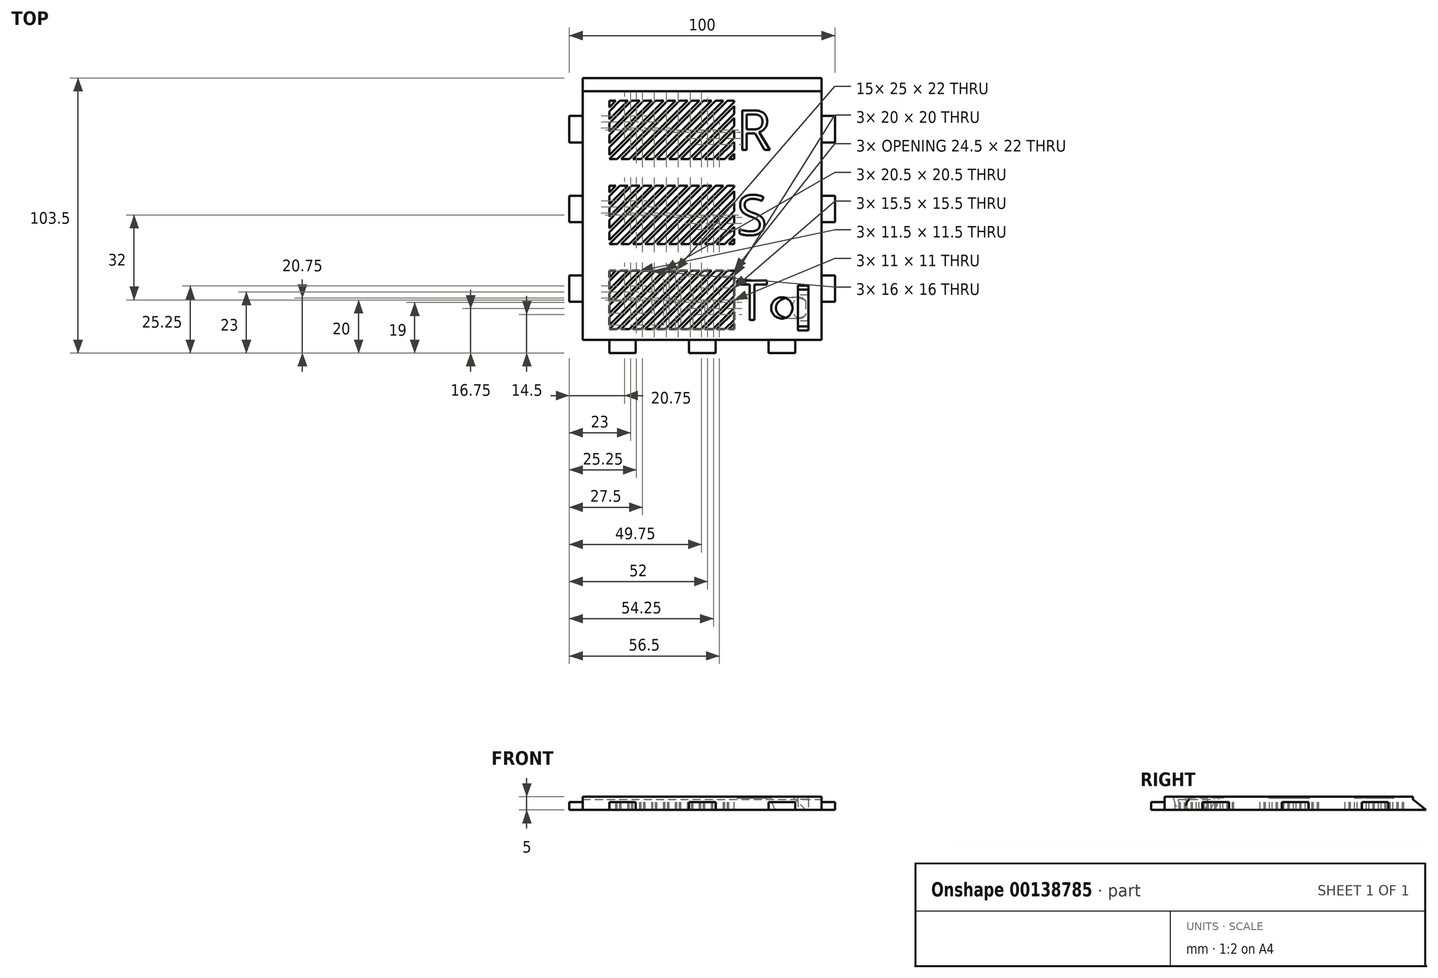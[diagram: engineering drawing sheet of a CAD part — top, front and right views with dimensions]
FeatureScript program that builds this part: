
annotation { "Feature Type Name" : "Feature", "Feature Type Description" : "" }
export const myFeature = defineFeature(function(context is Context, id is Id, definition is map)
    precondition{}
    {
        {
            var Q0;
            Q0=qCreatedBy(makeId("Top.planeOp"),FACE);
            var sketch = newSketch(context, id + "F0", { "sketchPlane" : qUnion([Q0])});
            skLineSegment(sketch, "E0.bottom", {"start": v(45, 49.25) * mm, "end": v(-45, 49.25) * mm});
            skLineSegment(sketch, "E0.top", {"start": v(45, -49.25) * mm, "end": v(-45, -49.25) * mm});
            skLineSegment(sketch, "E0.left", {"start": v(45, 49.25) * mm, "end": v(45, -49.25) * mm});
            skLineSegment(sketch, "E0.right", {"start": v(-45, 49.25) * mm, "end": v(-45, -49.25) * mm});
            skPoint(sketch, "E0.middle", {"position": v(0, 0) * mm});
            skSolve(sketch);
        }
        {
            var Q0;
            Q0 = qSketchRegion(id + "F0", true);
            extrude(context, id + "F1", {"entities" : qUnion([Q0]), "depth" : 5 * mm});
        }
        {
            var Q0;
            Q0=makeQuery(id+"F1.opExtrude","CAP_FACE",FACE,{"disambiguationData":[OSD([sQuery(id+"F0.wireOp",EDGE,"E0.bottom"),sQuery(id+"F0.wireOp",EDGE,"E0.top"),sQuery(id+"F0.wireOp",EDGE,"E0.left"),sQuery(id+"F0.wireOp",EDGE,"E0.right")])],"isStart":false});
            var sketch = newSketch(context, id + "F2", { "sketchPlane" : qUnion([Q0])});
            skLineSegment(sketch, "E1.bottom", {"start": v(-35, 40.75) * mm, "end": v(12, 40.75) * mm});
            skLineSegment(sketch, "E1.top", {"start": v(-35, 18.75) * mm, "end": v(12, 18.75) * mm});
            skLineSegment(sketch, "E1.left", {"start": v(-35, 40.75) * mm, "end": v(-35, 18.75) * mm});
            skLineSegment(sketch, "E1.right", {"start": v(12, 40.75) * mm, "end": v(12, 18.75) * mm});
            skLineSegment(sketch, "E2.bottom", {"start": v(-35, 8.75) * mm, "end": v(12, 8.75) * mm});
            skLineSegment(sketch, "E2.top", {"start": v(-35, -13.25) * mm, "end": v(12, -13.25) * mm});
            skLineSegment(sketch, "E2.left", {"start": v(-35, 8.75) * mm, "end": v(-35, -13.25) * mm});
            skLineSegment(sketch, "E2.right", {"start": v(12, 8.75) * mm, "end": v(12, -13.25) * mm});
            skLineSegment(sketch, "E3.bottom", {"start": v(-35, -23.25) * mm, "end": v(12, -23.25) * mm});
            skLineSegment(sketch, "E3.top", {"start": v(-35, -45.25) * mm, "end": v(12, -45.25) * mm});
            skLineSegment(sketch, "E3.left", {"start": v(-35, -23.25) * mm, "end": v(-35, -45.25) * mm});
            skLineSegment(sketch, "E3.right", {"start": v(12, -23.25) * mm, "end": v(12, -45.25) * mm});
            skSolve(sketch);
        }
        {
            var Q0;
            Q0=makeQuery(id+"F1.opExtrude","SWEPT_FACE",FACE,{"disambiguationData":[OSD([sQuery(id+"F0.wireOp",EDGE,"E0.right")])]});
            var sketch = newSketch(context, id + "F3", { "sketchPlane" : qUnion([Q0])});
            skLineSegment(sketch, "E4.bottom", {"start": v(-35, 0) * mm, "end": v(-25, 0) * mm});
            skLineSegment(sketch, "E4.top", {"start": v(-35, 3) * mm, "end": v(-25, 3) * mm});
            skLineSegment(sketch, "E4.left", {"start": v(-35, 0) * mm, "end": v(-35, 3) * mm});
            skLineSegment(sketch, "E4.right", {"start": v(-25, 0) * mm, "end": v(-25, 3) * mm});
            skLineSegment(sketch, "E5.bottom", {"start": v(-5, 0) * mm, "end": v(5, 0) * mm});
            skLineSegment(sketch, "E5.top", {"start": v(-5, 3) * mm, "end": v(5, 3) * mm});
            skLineSegment(sketch, "E5.left", {"start": v(-5, 0) * mm, "end": v(-5, 3) * mm});
            skLineSegment(sketch, "E5.right", {"start": v(5, 0) * mm, "end": v(5, 3) * mm});
            skLineSegment(sketch, "E6.bottom", {"start": v(25, 0) * mm, "end": v(35, 0) * mm});
            skLineSegment(sketch, "E6.top", {"start": v(25, 3) * mm, "end": v(35, 3) * mm});
            skLineSegment(sketch, "E6.left", {"start": v(25, 0) * mm, "end": v(25, 3) * mm});
            skLineSegment(sketch, "E6.right", {"start": v(35, 0) * mm, "end": v(35, 3) * mm});
            skSolve(sketch);
        }
        {
            var Q0;
            Q0 = qSketchRegion(id + "F3", true);
            extrude(context, id + "F4", {"entities" : qUnion([Q0]), "operationType" : NewBodyOperationType.ADD, "depth" : 5 * mm});
        }
        {
            var Q0;
            Q0=makeQuery(id+"F1.opExtrude","SWEPT_FACE",FACE,{"disambiguationData":[OSD([sQuery(id+"F0.wireOp",EDGE,"E0.left")])]});
            var sketch = newSketch(context, id + "F5", { "sketchPlane" : qUnion([Q0])});
            skLineSegment(sketch, "E7.bottom", {"start": v(-35, 3) * mm, "end": v(-25, 3) * mm});
            skLineSegment(sketch, "E7.top", {"start": v(-35, 0) * mm, "end": v(-25, 0) * mm});
            skLineSegment(sketch, "E7.left", {"start": v(-35, 3) * mm, "end": v(-35, 0) * mm});
            skLineSegment(sketch, "E7.right", {"start": v(-25, 3) * mm, "end": v(-25, 0) * mm});
            skLineSegment(sketch, "E8.bottom", {"start": v(-5, 3) * mm, "end": v(5, 3) * mm});
            skLineSegment(sketch, "E8.top", {"start": v(-5, 0) * mm, "end": v(5, 0) * mm});
            skLineSegment(sketch, "E8.left", {"start": v(-5, 3) * mm, "end": v(-5, 0) * mm});
            skLineSegment(sketch, "E8.right", {"start": v(5, 3) * mm, "end": v(5, 0) * mm});
            skLineSegment(sketch, "E9.bottom", {"start": v(25, 3) * mm, "end": v(35, 3) * mm});
            skLineSegment(sketch, "E9.top", {"start": v(25, 0) * mm, "end": v(35, 0) * mm});
            skLineSegment(sketch, "E9.left", {"start": v(25, 3) * mm, "end": v(25, 0) * mm});
            skLineSegment(sketch, "E9.right", {"start": v(35, 3) * mm, "end": v(35, 0) * mm});
            skSolve(sketch);
        }
        {
            var Q0;
            Q0 = qSketchRegion(id + "F5", true);
            extrude(context, id + "F6", {"entities" : qUnion([Q0]), "operationType" : NewBodyOperationType.ADD, "depth" : 5 * mm});
        }
        {
            var Q0;
            Q0=makeQuery(id+"F1.opExtrude","SWEPT_FACE",FACE,{"disambiguationData":[OSD([sQuery(id+"F0.wireOp",EDGE,"E0.top")])]});
            var sketch = newSketch(context, id + "F7", { "sketchPlane" : qUnion([Q0])});
            skLineSegment(sketch, "E10.bottom", {"start": v(-35, 0) * mm, "end": v(-25, 0) * mm});
            skLineSegment(sketch, "E10.top", {"start": v(-35, 3) * mm, "end": v(-25, 3) * mm});
            skLineSegment(sketch, "E10.left", {"start": v(-35, 0) * mm, "end": v(-35, 3) * mm});
            skLineSegment(sketch, "E10.right", {"start": v(-25, 0) * mm, "end": v(-25, 3) * mm});
            skLineSegment(sketch, "E11.bottom", {"start": v(-5, 0) * mm, "end": v(5, 0) * mm});
            skLineSegment(sketch, "E11.top", {"start": v(-5, 3) * mm, "end": v(5, 3) * mm});
            skLineSegment(sketch, "E11.left", {"start": v(-5, 0) * mm, "end": v(-5, 3) * mm});
            skLineSegment(sketch, "E11.right", {"start": v(5, 0) * mm, "end": v(5, 3) * mm});
            skLineSegment(sketch, "E12.bottom", {"start": v(25, 0) * mm, "end": v(35, 0) * mm});
            skLineSegment(sketch, "E12.top", {"start": v(25, 3) * mm, "end": v(35, 3) * mm});
            skLineSegment(sketch, "E12.left", {"start": v(25, 0) * mm, "end": v(25, 3) * mm});
            skLineSegment(sketch, "E12.right", {"start": v(35, 0) * mm, "end": v(35, 3) * mm});
            skSolve(sketch);
        }
        {
            var Q0;
            Q0 = qSketchRegion(id + "F7", true);
            extrude(context, id + "F8", {"entities" : qUnion([Q0]), "operationType" : NewBodyOperationType.ADD, "depth" : 5 * mm});
        }
        {
            var Q0;
            Q0=makeQuery(id+"F2.imprint","IMPRINT",FACE,{"disambiguationData":[TD([[makeQuery(id+"F2.imprint","IMPRINT",EDGE,{"derivedFrom":sQuery(id+"F2.wireOp",EDGE,"E1.bottom")}),-1.0]])]});
            var sketch = newSketch(context, id + "F9", { "sketchPlane" : qUnion([Q0])});
            skLineSegment(sketch, "E13", {"start": v(-35, 18.75) * mm, "end": v(-13, 40.75) * mm});
            skLineSegment(sketch, "E14", {"start": v(-13, 40.75) * mm, "end": v(-10, 40.75) * mm});
            skLineSegment(sketch, "E15", {"start": v(-10, 40.75) * mm, "end": v(-32, 18.75) * mm});
            skLineSegment(sketch, "E16", {"start": v(-32, 18.75) * mm, "end": v(-35, 18.75) * mm});
            skLineSegment(sketch, "E17.1.0.0", {"start": v(-27.5, 18.75) * mm, "end": v(-30.5, 18.75) * mm});
            skLineSegment(sketch, "E17.1.0.1", {"start": v(-5.5, 40.75) * mm, "end": v(-27.5, 18.75) * mm});
            skLineSegment(sketch, "E17.1.0.2", {"start": v(-8.5, 40.75) * mm, "end": v(-5.5, 40.75) * mm});
            skLineSegment(sketch, "E17.1.0.3", {"start": v(-30.5, 18.75) * mm, "end": v(-8.5, 40.75) * mm});
            skLineSegment(sketch, "E17.2.0.0", {"start": v(-23, 18.75) * mm, "end": v(-26, 18.75) * mm});
            skLineSegment(sketch, "E17.2.0.1", {"start": v(-1, 40.75) * mm, "end": v(-23, 18.75) * mm});
            skLineSegment(sketch, "E17.2.0.2", {"start": v(-4, 40.75) * mm, "end": v(-1, 40.75) * mm});
            skLineSegment(sketch, "E17.2.0.3", {"start": v(-26, 18.75) * mm, "end": v(-4, 40.75) * mm});
            skLineSegment(sketch, "E17.3.0.0", {"start": v(-18.5, 18.75) * mm, "end": v(-21.5, 18.75) * mm});
            skLineSegment(sketch, "E17.3.0.1", {"start": v(3.5, 40.75) * mm, "end": v(-18.5, 18.75) * mm});
            skLineSegment(sketch, "E17.3.0.2", {"start": v(0.5, 40.75) * mm, "end": v(3.5, 40.75) * mm});
            skLineSegment(sketch, "E17.3.0.3", {"start": v(-21.5, 18.75) * mm, "end": v(0.5, 40.75) * mm});
            skLineSegment(sketch, "E17.4.0.0", {"start": v(-14, 18.75) * mm, "end": v(-17, 18.75) * mm});
            skLineSegment(sketch, "E17.4.0.1", {"start": v(8, 40.75) * mm, "end": v(-14, 18.75) * mm});
            skLineSegment(sketch, "E17.4.0.2", {"start": v(5, 40.75) * mm, "end": v(8, 40.75) * mm});
            skLineSegment(sketch, "E17.4.0.3", {"start": v(-17, 18.75) * mm, "end": v(5, 40.75) * mm});
            skLineSegment(sketch, "E17.5.0.0", {"start": v(-9.5, 18.75) * mm, "end": v(-12.5, 18.75) * mm});
            skLineSegment(sketch, "E17.5.0.1", {"start": v(12, 40.25) * mm, "end": v(-9.5, 18.75) * mm});
            skLineSegment(sketch, "E17.5.0.2", {"start": v(9.5, 40.75) * mm, "end": v(12, 40.75) * mm});
            skLineSegment(sketch, "E17.5.0.3", {"start": v(-12.5, 18.75) * mm, "end": v(9.5, 40.75) * mm});
            skLineSegment(sketch, "E17.6.0.0", {"start": v(-5, 18.75) * mm, "end": v(-8, 18.75) * mm});
            skLineSegment(sketch, "E17.6.0.1", {"start": v(12, 35.75) * mm, "end": v(-5, 18.75) * mm});
            skLineSegment(sketch, "E17.6.0.3", {"start": v(-8, 18.75) * mm, "end": v(12, 38.75) * mm});
            skLineSegment(sketch, "E17.7.0.0", {"start": v(-0.5, 18.75) * mm, "end": v(-3.5, 18.75) * mm});
            skLineSegment(sketch, "E17.7.0.1", {"start": v(12, 31.25) * mm, "end": v(-0.5, 18.75) * mm});
            skLineSegment(sketch, "E17.7.0.3", {"start": v(-3.5, 18.75) * mm, "end": v(12, 34.25) * mm});
            skLineSegment(sketch, "E17.8.0.0", {"start": v(4, 18.75) * mm, "end": v(1, 18.75) * mm});
            skLineSegment(sketch, "E17.8.0.1", {"start": v(12, 26.75) * mm, "end": v(4, 18.75) * mm});
            skLineSegment(sketch, "E17.8.0.3", {"start": v(1, 18.75) * mm, "end": v(12, 29.75) * mm});
            skLineSegment(sketch, "E17.9.0.0", {"start": v(8.5, 18.75) * mm, "end": v(5.5, 18.75) * mm});
            skLineSegment(sketch, "E17.9.0.1", {"start": v(12, 22.25) * mm, "end": v(8.5, 18.75) * mm});
            skLineSegment(sketch, "E17.9.0.3", {"start": v(5.5, 18.75) * mm, "end": v(12, 25.25) * mm});
            skLineSegment(sketch, "E17.10.0.0", {"start": v(12, 18.75) * mm, "end": v(10, 18.75) * mm});
            skLineSegment(sketch, "E17.10.0.3", {"start": v(10, 18.75) * mm, "end": v(12, 20.75) * mm});
            skLineSegment(sketch, "E17.direction1", {"start": v(-35, 18.75) * mm, "end": v(-30.5, 18.75) * mm, "construction": true});
            skLineSegment(sketch, "E18.left", {"start": v(-35, 20.25) * mm, "end": v(-35, 23.25) * mm});
            skLineSegment(sketch, "E18.right", {"start": v(12, 18.75) * mm, "end": v(12, 20.75) * mm});
            skLineSegment(sketch, "E19.1.0.0", {"start": v(-17.5, 40.75) * mm, "end": v(-14.5, 40.75) * mm});
            skLineSegment(sketch, "E19.1.0.1", {"start": v(-14.5, 40.75) * mm, "end": v(-35, 20.25) * mm});
            skLineSegment(sketch, "E19.1.0.2", {"start": v(-35, 23.25) * mm, "end": v(-17.5, 40.75) * mm});
            skLineSegment(sketch, "E19.2.0.0", {"start": v(-22, 40.75) * mm, "end": v(-19, 40.75) * mm});
            skLineSegment(sketch, "E19.2.0.1", {"start": v(-19, 40.75) * mm, "end": v(-35, 24.75) * mm});
            skLineSegment(sketch, "E19.2.0.2", {"start": v(-35, 27.75) * mm, "end": v(-22, 40.75) * mm});
            skLineSegment(sketch, "E19.3.0.0", {"start": v(-26.5, 40.75) * mm, "end": v(-23.5, 40.75) * mm});
            skLineSegment(sketch, "E19.3.0.1", {"start": v(-23.5, 40.75) * mm, "end": v(-35, 29.25) * mm});
            skLineSegment(sketch, "E19.3.0.2", {"start": v(-35, 32.25) * mm, "end": v(-26.5, 40.75) * mm});
            skLineSegment(sketch, "E19.4.0.0", {"start": v(-31, 40.75) * mm, "end": v(-28, 40.75) * mm});
            skLineSegment(sketch, "E19.4.0.1", {"start": v(-28, 40.75) * mm, "end": v(-35, 33.75) * mm});
            skLineSegment(sketch, "E19.4.0.2", {"start": v(-35, 36.75) * mm, "end": v(-31, 40.75) * mm});
            skLineSegment(sketch, "E19.5.0.0", {"start": v(-35, 40.75) * mm, "end": v(-32.5, 40.75) * mm});
            skLineSegment(sketch, "E19.5.0.1", {"start": v(-32.5, 40.75) * mm, "end": v(-35, 38.25) * mm});
            skLineSegment(sketch, "E19.direction1", {"start": v(-35, 18.75) * mm, "end": v(-39.5, 18.75) * mm, "construction": true});
            skLineSegment(sketch, "E20.trimOffspring", {"start": v(-35, 24.75) * mm, "end": v(-35, 27.75) * mm});
            skLineSegment(sketch, "E21.trimOffspring", {"start": v(-35, 29.25) * mm, "end": v(-35, 32.25) * mm});
            skLineSegment(sketch, "E22.trimOffspring", {"start": v(-35, 33.75) * mm, "end": v(-35, 36.75) * mm});
            skLineSegment(sketch, "E23.trimOffspring", {"start": v(-35, 38.25) * mm, "end": v(-35, 40.75) * mm});
            skLineSegment(sketch, "E24.trimOffspring", {"start": v(12, 40.25) * mm, "end": v(12, 40.75) * mm});
            skLineSegment(sketch, "E25.trimOffspring", {"start": v(12, 35.75) * mm, "end": v(12, 38.75) * mm});
            skLineSegment(sketch, "E26.trimOffspring", {"start": v(12, 31.25) * mm, "end": v(12, 34.25) * mm});
            skLineSegment(sketch, "E27.trimOffspring", {"start": v(12, 26.75) * mm, "end": v(12, 29.75) * mm});
            skLineSegment(sketch, "E28.trimOffspring", {"start": v(12, 22.25) * mm, "end": v(12, 25.25) * mm});
            skLineSegment(sketch, "E29.0.1.0", {"start": v(-35, -4.25) * mm, "end": v(-22, 8.75) * mm});
            skLineSegment(sketch, "E29.0.1.1", {"start": v(-3.5, -13.25) * mm, "end": v(12, 2.25) * mm});
            skLineSegment(sketch, "E29.0.1.2", {"start": v(-30.5, -13.25) * mm, "end": v(-8.5, 8.75) * mm});
            skLineSegment(sketch, "E29.0.1.3", {"start": v(-17, -13.25) * mm, "end": v(5, 8.75) * mm});
            skLineSegment(sketch, "E29.0.1.4", {"start": v(-23.5, 8.75) * mm, "end": v(-35, -2.75) * mm});
            skLineSegment(sketch, "E29.0.1.5", {"start": v(12, 8.25) * mm, "end": v(-9.5, -13.25) * mm});
            skLineSegment(sketch, "E29.0.1.6", {"start": v(12, -0.75) * mm, "end": v(-0.5, -13.25) * mm});
            skLineSegment(sketch, "E29.0.1.7", {"start": v(-8, -13.25) * mm, "end": v(12, 6.75) * mm});
            skLineSegment(sketch, "E29.0.1.8", {"start": v(-14.5, 8.75) * mm, "end": v(-35, -11.75) * mm});
            skLineSegment(sketch, "E29.0.1.9", {"start": v(-26, -13.25) * mm, "end": v(-4, 8.75) * mm});
            skLineSegment(sketch, "E29.0.1.10", {"start": v(-19, 8.75) * mm, "end": v(-35, -7.25) * mm});
            skLineSegment(sketch, "E29.0.1.11", {"start": v(5.5, -13.25) * mm, "end": v(12, -6.75) * mm});
            skLineSegment(sketch, "E29.0.1.12", {"start": v(-10, 8.75) * mm, "end": v(-32, -13.25) * mm});
            skLineSegment(sketch, "E29.0.1.13", {"start": v(-35, -8.75) * mm, "end": v(-17.5, 8.75) * mm});
            skLineSegment(sketch, "E29.0.1.14", {"start": v(-1, 8.75) * mm, "end": v(-23, -13.25) * mm});
            skLineSegment(sketch, "E29.0.1.15", {"start": v(-35, 4.75) * mm, "end": v(-31, 8.75) * mm});
            skLineSegment(sketch, "E29.0.1.16", {"start": v(-35, -13.25) * mm, "end": v(-13, 8.75) * mm});
            skLineSegment(sketch, "E29.0.1.17", {"start": v(-5.5, 8.75) * mm, "end": v(-27.5, -13.25) * mm});
            skLineSegment(sketch, "E29.0.1.18", {"start": v(-28, 8.75) * mm, "end": v(-35, 1.75) * mm});
            skLineSegment(sketch, "E29.0.1.19", {"start": v(-21.5, -13.25) * mm, "end": v(0.5, 8.75) * mm});
            skLineSegment(sketch, "E29.0.1.20", {"start": v(3.5, 8.75) * mm, "end": v(-18.5, -13.25) * mm});
            skLineSegment(sketch, "E29.0.1.21", {"start": v(12, -5.25) * mm, "end": v(4, -13.25) * mm});
            skLineSegment(sketch, "E29.0.1.22", {"start": v(1, -13.25) * mm, "end": v(12, -2.25) * mm});
            skLineSegment(sketch, "E29.0.1.23", {"start": v(-12.5, -13.25) * mm, "end": v(9.5, 8.75) * mm});
            skLineSegment(sketch, "E29.0.1.24", {"start": v(-35, 0.25) * mm, "end": v(-26.5, 8.75) * mm});
            skLineSegment(sketch, "E29.0.1.25", {"start": v(8, 8.75) * mm, "end": v(-14, -13.25) * mm});
            skLineSegment(sketch, "E29.0.1.26", {"start": v(12, -9.75) * mm, "end": v(8.5, -13.25) * mm});
            skLineSegment(sketch, "E29.0.1.27", {"start": v(12, 3.75) * mm, "end": v(-5, -13.25) * mm});
            skLineSegment(sketch, "E29.0.1.28", {"start": v(-32.5, 8.75) * mm, "end": v(-35, 6.25) * mm});
            skLineSegment(sketch, "E29.0.1.29", {"start": v(-26.5, 8.75) * mm, "end": v(-23.5, 8.75) * mm});
            skLineSegment(sketch, "E29.0.1.30", {"start": v(12, -5.25) * mm, "end": v(12, -2.25) * mm});
            skLineSegment(sketch, "E29.0.1.31", {"start": v(4, -13.25) * mm, "end": v(1, -13.25) * mm});
            skLineSegment(sketch, "E29.0.1.32", {"start": v(-35, 8.75) * mm, "end": v(-32.5, 8.75) * mm});
            skLineSegment(sketch, "E29.0.1.33", {"start": v(12, -0.75) * mm, "end": v(12, 2.25) * mm});
            skLineSegment(sketch, "E29.0.1.34", {"start": v(-4, 8.75) * mm, "end": v(-1, 8.75) * mm});
            skLineSegment(sketch, "E29.0.1.35", {"start": v(-23, -13.25) * mm, "end": v(-26, -13.25) * mm});
            skLineSegment(sketch, "E29.0.1.36", {"start": v(9.5, 8.75) * mm, "end": v(12, 8.75) * mm});
            skLineSegment(sketch, "E29.0.1.37", {"start": v(-27.5, -13.25) * mm, "end": v(-30.5, -13.25) * mm});
            skLineSegment(sketch, "E29.0.1.38", {"start": v(10, -13.25) * mm, "end": v(12, -11.25) * mm});
            skLineSegment(sketch, "E29.0.1.39", {"start": v(-22, 8.75) * mm, "end": v(-19, 8.75) * mm});
            skLineSegment(sketch, "E29.0.1.40", {"start": v(-35, 1.75) * mm, "end": v(-35, 4.75) * mm});
            skLineSegment(sketch, "E29.0.1.41", {"start": v(-18.5, -13.25) * mm, "end": v(-21.5, -13.25) * mm});
            skLineSegment(sketch, "E29.0.1.42", {"start": v(-9.5, -13.25) * mm, "end": v(-12.5, -13.25) * mm});
            skLineSegment(sketch, "E29.0.1.43", {"start": v(-35, 6.25) * mm, "end": v(-35, 8.75) * mm});
            skLineSegment(sketch, "E29.0.1.44", {"start": v(-0.5, -13.25) * mm, "end": v(-3.5, -13.25) * mm});
            skLineSegment(sketch, "E29.0.1.45", {"start": v(-13, 8.75) * mm, "end": v(-10, 8.75) * mm});
            skLineSegment(sketch, "E29.0.1.46", {"start": v(12, 3.75) * mm, "end": v(12, 6.75) * mm});
            skLineSegment(sketch, "E29.0.1.47", {"start": v(-8.5, 8.75) * mm, "end": v(-5.5, 8.75) * mm});
            skLineSegment(sketch, "E29.0.1.48", {"start": v(0.5, 8.75) * mm, "end": v(3.5, 8.75) * mm});
            skLineSegment(sketch, "E29.0.1.49", {"start": v(12, -9.75) * mm, "end": v(12, -6.75) * mm});
            skLineSegment(sketch, "E29.0.1.50", {"start": v(-35, -13.25) * mm, "end": v(-30.5, -13.25) * mm, "construction": true});
            skLineSegment(sketch, "E29.0.1.51", {"start": v(-14, -13.25) * mm, "end": v(-17, -13.25) * mm});
            skLineSegment(sketch, "E29.0.1.52", {"start": v(-35, -11.75) * mm, "end": v(-35, -8.75) * mm});
            skLineSegment(sketch, "E29.0.1.53", {"start": v(8.5, -13.25) * mm, "end": v(5.5, -13.25) * mm});
            skLineSegment(sketch, "E29.0.1.54", {"start": v(12, -13.25) * mm, "end": v(12, -11.25) * mm});
            skLineSegment(sketch, "E29.0.1.55", {"start": v(-5, -13.25) * mm, "end": v(-8, -13.25) * mm});
            skLineSegment(sketch, "E29.0.1.56", {"start": v(-35, -7.25) * mm, "end": v(-35, -4.25) * mm});
            skLineSegment(sketch, "E29.0.1.57", {"start": v(-31, 8.75) * mm, "end": v(-28, 8.75) * mm});
            skLineSegment(sketch, "E29.0.1.58", {"start": v(5, 8.75) * mm, "end": v(8, 8.75) * mm});
            skLineSegment(sketch, "E29.0.1.59", {"start": v(-17.5, 8.75) * mm, "end": v(-14.5, 8.75) * mm});
            skLineSegment(sketch, "E29.0.1.60", {"start": v(-35, -2.75) * mm, "end": v(-35, 0.25) * mm});
            skLineSegment(sketch, "E29.0.1.61", {"start": v(12, -13.25) * mm, "end": v(10, -13.25) * mm});
            skLineSegment(sketch, "E29.0.1.62", {"start": v(-32, -13.25) * mm, "end": v(-35, -13.25) * mm});
            skLineSegment(sketch, "E29.0.1.63", {"start": v(12, 8.25) * mm, "end": v(12, 8.75) * mm});
            skLineSegment(sketch, "E29.0.2.0", {"start": v(-35, -36.25) * mm, "end": v(-22, -23.25) * mm});
            skLineSegment(sketch, "E29.0.2.1", {"start": v(-3.5, -45.25) * mm, "end": v(12, -29.75) * mm});
            skLineSegment(sketch, "E29.0.2.2", {"start": v(-30.5, -45.25) * mm, "end": v(-8.5, -23.25) * mm});
            skLineSegment(sketch, "E29.0.2.3", {"start": v(-17, -45.25) * mm, "end": v(5, -23.25) * mm});
            skLineSegment(sketch, "E29.0.2.4", {"start": v(-23.5, -23.25) * mm, "end": v(-35, -34.75) * mm});
            skLineSegment(sketch, "E29.0.2.5", {"start": v(12, -23.75) * mm, "end": v(-9.5, -45.25) * mm});
            skLineSegment(sketch, "E29.0.2.6", {"start": v(12, -32.75) * mm, "end": v(-0.5, -45.25) * mm});
            skLineSegment(sketch, "E29.0.2.7", {"start": v(-8, -45.25) * mm, "end": v(12, -25.25) * mm});
            skLineSegment(sketch, "E29.0.2.8", {"start": v(-14.5, -23.25) * mm, "end": v(-35, -43.75) * mm});
            skLineSegment(sketch, "E29.0.2.9", {"start": v(-26, -45.25) * mm, "end": v(-4, -23.25) * mm});
            skLineSegment(sketch, "E29.0.2.10", {"start": v(-19, -23.25) * mm, "end": v(-35, -39.25) * mm});
            skLineSegment(sketch, "E29.0.2.11", {"start": v(5.5, -45.25) * mm, "end": v(12, -38.75) * mm});
            skLineSegment(sketch, "E29.0.2.12", {"start": v(-10, -23.25) * mm, "end": v(-32, -45.25) * mm});
            skLineSegment(sketch, "E29.0.2.13", {"start": v(-35, -40.75) * mm, "end": v(-17.5, -23.25) * mm});
            skLineSegment(sketch, "E29.0.2.14", {"start": v(-1, -23.25) * mm, "end": v(-23, -45.25) * mm});
            skLineSegment(sketch, "E29.0.2.15", {"start": v(-35, -27.25) * mm, "end": v(-31, -23.25) * mm});
            skLineSegment(sketch, "E29.0.2.16", {"start": v(-35, -45.25) * mm, "end": v(-13, -23.25) * mm});
            skLineSegment(sketch, "E29.0.2.17", {"start": v(-5.5, -23.25) * mm, "end": v(-27.5, -45.25) * mm});
            skLineSegment(sketch, "E29.0.2.18", {"start": v(-28, -23.25) * mm, "end": v(-35, -30.25) * mm});
            skLineSegment(sketch, "E29.0.2.19", {"start": v(-21.5, -45.25) * mm, "end": v(0.5, -23.25) * mm});
            skLineSegment(sketch, "E29.0.2.20", {"start": v(3.5, -23.25) * mm, "end": v(-18.5, -45.25) * mm});
            skLineSegment(sketch, "E29.0.2.21", {"start": v(12, -37.25) * mm, "end": v(4, -45.25) * mm});
            skLineSegment(sketch, "E29.0.2.22", {"start": v(1, -45.25) * mm, "end": v(12, -34.25) * mm});
            skLineSegment(sketch, "E29.0.2.23", {"start": v(-12.5, -45.25) * mm, "end": v(9.5, -23.25) * mm});
            skLineSegment(sketch, "E29.0.2.24", {"start": v(-35, -31.75) * mm, "end": v(-26.5, -23.25) * mm});
            skLineSegment(sketch, "E29.0.2.25", {"start": v(8, -23.25) * mm, "end": v(-14, -45.25) * mm});
            skLineSegment(sketch, "E29.0.2.26", {"start": v(12, -41.75) * mm, "end": v(8.5, -45.25) * mm});
            skLineSegment(sketch, "E29.0.2.27", {"start": v(12, -28.25) * mm, "end": v(-5, -45.25) * mm});
            skLineSegment(sketch, "E29.0.2.28", {"start": v(-32.5, -23.25) * mm, "end": v(-35, -25.75) * mm});
            skLineSegment(sketch, "E29.0.2.29", {"start": v(-26.5, -23.25) * mm, "end": v(-23.5, -23.25) * mm});
            skLineSegment(sketch, "E29.0.2.30", {"start": v(12, -37.25) * mm, "end": v(12, -34.25) * mm});
            skLineSegment(sketch, "E29.0.2.31", {"start": v(4, -45.25) * mm, "end": v(1, -45.25) * mm});
            skLineSegment(sketch, "E29.0.2.32", {"start": v(-35, -23.25) * mm, "end": v(-32.5, -23.25) * mm});
            skLineSegment(sketch, "E29.0.2.33", {"start": v(12, -32.75) * mm, "end": v(12, -29.75) * mm});
            skLineSegment(sketch, "E29.0.2.34", {"start": v(-4, -23.25) * mm, "end": v(-1, -23.25) * mm});
            skLineSegment(sketch, "E29.0.2.35", {"start": v(-23, -45.25) * mm, "end": v(-26, -45.25) * mm});
            skLineSegment(sketch, "E29.0.2.36", {"start": v(9.5, -23.25) * mm, "end": v(12, -23.25) * mm});
            skLineSegment(sketch, "E29.0.2.37", {"start": v(-27.5, -45.25) * mm, "end": v(-30.5, -45.25) * mm});
            skLineSegment(sketch, "E29.0.2.38", {"start": v(10, -45.25) * mm, "end": v(12, -43.25) * mm});
            skLineSegment(sketch, "E29.0.2.39", {"start": v(-22, -23.25) * mm, "end": v(-19, -23.25) * mm});
            skLineSegment(sketch, "E29.0.2.40", {"start": v(-35, -30.25) * mm, "end": v(-35, -27.25) * mm});
            skLineSegment(sketch, "E29.0.2.41", {"start": v(-18.5, -45.25) * mm, "end": v(-21.5, -45.25) * mm});
            skLineSegment(sketch, "E29.0.2.42", {"start": v(-9.5, -45.25) * mm, "end": v(-12.5, -45.25) * mm});
            skLineSegment(sketch, "E29.0.2.43", {"start": v(-35, -25.75) * mm, "end": v(-35, -23.25) * mm});
            skLineSegment(sketch, "E29.0.2.44", {"start": v(-0.5, -45.25) * mm, "end": v(-3.5, -45.25) * mm});
            skLineSegment(sketch, "E29.0.2.45", {"start": v(-13, -23.25) * mm, "end": v(-10, -23.25) * mm});
            skLineSegment(sketch, "E29.0.2.46", {"start": v(12, -28.25) * mm, "end": v(12, -25.25) * mm});
            skLineSegment(sketch, "E29.0.2.47", {"start": v(-8.5, -23.25) * mm, "end": v(-5.5, -23.25) * mm});
            skLineSegment(sketch, "E29.0.2.48", {"start": v(0.5, -23.25) * mm, "end": v(3.5, -23.25) * mm});
            skLineSegment(sketch, "E29.0.2.49", {"start": v(12, -41.75) * mm, "end": v(12, -38.75) * mm});
            skLineSegment(sketch, "E29.0.2.50", {"start": v(-35, -45.25) * mm, "end": v(-30.5, -45.25) * mm, "construction": true});
            skLineSegment(sketch, "E29.0.2.51", {"start": v(-14, -45.25) * mm, "end": v(-17, -45.25) * mm});
            skLineSegment(sketch, "E29.0.2.52", {"start": v(-35, -43.75) * mm, "end": v(-35, -40.75) * mm});
            skLineSegment(sketch, "E29.0.2.53", {"start": v(8.5, -45.25) * mm, "end": v(5.5, -45.25) * mm});
            skLineSegment(sketch, "E29.0.2.54", {"start": v(12, -45.25) * mm, "end": v(12, -43.25) * mm});
            skLineSegment(sketch, "E29.0.2.55", {"start": v(-5, -45.25) * mm, "end": v(-8, -45.25) * mm});
            skLineSegment(sketch, "E29.0.2.56", {"start": v(-35, -39.25) * mm, "end": v(-35, -36.25) * mm});
            skLineSegment(sketch, "E29.0.2.57", {"start": v(-31, -23.25) * mm, "end": v(-28, -23.25) * mm});
            skLineSegment(sketch, "E29.0.2.58", {"start": v(5, -23.25) * mm, "end": v(8, -23.25) * mm});
            skLineSegment(sketch, "E29.0.2.59", {"start": v(-17.5, -23.25) * mm, "end": v(-14.5, -23.25) * mm});
            skLineSegment(sketch, "E29.0.2.60", {"start": v(-35, -34.75) * mm, "end": v(-35, -31.75) * mm});
            skLineSegment(sketch, "E29.0.2.61", {"start": v(12, -45.25) * mm, "end": v(10, -45.25) * mm});
            skLineSegment(sketch, "E29.0.2.62", {"start": v(-32, -45.25) * mm, "end": v(-35, -45.25) * mm});
            skLineSegment(sketch, "E29.0.2.63", {"start": v(12, -23.75) * mm, "end": v(12, -23.25) * mm});
            skLineSegment(sketch, "E29.direction1", {"start": v(-35, 18.75) * mm, "end": v(-10, 18.75) * mm, "construction": true});
            skLineSegment(sketch, "E29.direction2", {"start": v(-35, 18.75) * mm, "end": v(-35, -13.25) * mm, "construction": true});
            skSolve(sketch);
        }
        {
            var Q0;
            Q0 = qSketchRegion(id + "F9", true);
            extrude(context, id + "F10", {"entities" : qUnion([Q0]), "operationType" : NewBodyOperationType.REMOVE, "oppositeDirection" : true, "depth" : 25 * mm});
        }
        {
            var Q0;
            Q0=makeQuery(id+"F1.opExtrude","CAP_FACE",FACE,{"disambiguationData":[OSD([sQuery(id+"F0.wireOp",EDGE,"E0.bottom"),sQuery(id+"F0.wireOp",EDGE,"E0.top"),sQuery(id+"F0.wireOp",EDGE,"E0.left"),sQuery(id+"F0.wireOp",EDGE,"E0.right")])],"isStart":false});
            var sketch = newSketch(context, id + "F11", { "sketchPlane" : qUnion([Q0])});
            skText(sketch, "E30", { "text": "R", "fontName": "OpenSans-Regular.ttf"});
            skText(sketch, "E31", { "text": "S\n", "fontName": "OpenSans-Regular.ttf"});
            skText(sketch, "E32", { "text": "T", "fontName": "OpenSans-Regular.ttf"});
            const initialGuessF11  = {"E30": [0.013, 0.02225, 1, 0, 0.015], "E31": [0.013, -0.00975, 1, 0, 0.015], "E32": [0.013, -0.04175, 1, 0, 0.015]};
            skSetInitialGuess(sketch, initialGuessF11);
            skSolve(sketch);
        }
        {
            var Q0;
            Q0 = qSketchRegion(id + "F11", true);
            extrude(context, id + "F12", {"entities" : qUnion([Q0]), "operationType" : NewBodyOperationType.REMOVE, "oppositeDirection" : true, "depth" : 0.5 * mm});
        }
        {
            var Q0;
            {var subQ0=sQuery(id+"F0.wireOp",EDGE,"E0.right");var subQ1=sQuery(id+"F0.wireOp",EDGE,"E0.left");var subQ2=sQuery(id+"F0.wireOp",EDGE,"E0.bottom");var subQ3=sQuery(id+"F0.wireOp",EDGE,"E0.top");Q0=makeQuery(id+"F12.boolean.opBoolean","SPLIT",FACE,{"disambiguationData":[TD([makeQuery(id+"F1.opExtrude","SWEPT_FACE",FACE,{"disambiguationData":[OSD([subQ2])]})])],"derivedFrom":makeQuery(id+"F1.opExtrude","CAP_FACE",FACE,{"disambiguationData":[OSD([subQ2,subQ3,subQ1,subQ0])],"isStart":false})});}
            var sketch = newSketch(context, id + "F13", { "sketchPlane" : qUnion([Q0])});
            skCircle(sketch, "E33", {"center": v(30, -37.27) * mm, "radius": 4 * mm});
            skLineSegment(sketch, "E34", {"start": v(34, -49.25) * mm, "end": v(34, -34.45) * mm});
            skSolve(sketch);
        }
        {
            var Q0;
            Q0=makeQuery(id+"F13.imprint","IMPRINT",FACE,{"disambiguationData":[TD([[makeQuery(id+"F13.imprint","IMPRINT",EDGE,{"derivedFrom":sQuery(id+"F13.wireOp",EDGE,"E33")}),1.0]])]});
            var Q1;
            Q1=sQuery(id+"F13.wireOp",EDGE,"E34");
            revolve(context, id + "F14", {"operationType" : NewBodyOperationType.REMOVE, "entities" : qUnion([Q0]), "axis" : qUnion([Q1]), "revolveType" : RevolveType.ONE_DIRECTION, "oppositeDirection" : true, "angle" : 135 * degree});
        }
        {
            var Q0;
            {var subQ0=sQuery(id+"F0.wireOp",EDGE,"E0.right");var subQ1=sQuery(id+"F0.wireOp",EDGE,"E0.left");var subQ2=sQuery(id+"F0.wireOp",EDGE,"E0.bottom");var subQ3=sQuery(id+"F0.wireOp",EDGE,"E0.top");Q0=makeQuery(id+"F12.boolean.opBoolean","SPLIT",FACE,{"disambiguationData":[TD([makeQuery(id+"F1.opExtrude","SWEPT_FACE",FACE,{"disambiguationData":[OSD([subQ2])]})])],"derivedFrom":makeQuery(id+"F1.opExtrude","CAP_FACE",FACE,{"disambiguationData":[OSD([subQ2,subQ3,subQ1,subQ0])],"isStart":false})});}
            var sketch = newSketch(context, id + "F15", { "sketchPlane" : qUnion([Q0])});
            skLineSegment(sketch, "E35.bottom", {"start": v(36, -28.77) * mm, "end": v(40, -28.77) * mm});
            skLineSegment(sketch, "E35.top", {"start": v(36, -30.27) * mm, "end": v(40, -30.27) * mm});
            skLineSegment(sketch, "E35.left", {"start": v(36, -28.77) * mm, "end": v(36, -30.27) * mm});
            skLineSegment(sketch, "E35.right", {"start": v(40, -28.77) * mm, "end": v(40, -30.27) * mm});
            skLineSegment(sketch, "E36", {"start": v(34, -37.27) * mm, "end": v(47.47, -37.27) * mm});
            skSolve(sketch);
        }
        {
            var Q0;
            Q0=makeQuery(id+"F15.imprint","IMPRINT",FACE,{"disambiguationData":[TD([[makeQuery(id+"F15.imprint","IMPRINT",EDGE,{"derivedFrom":sQuery(id+"F15.wireOp",EDGE,"E35.bottom")}),-1.0]])]});
            var Q1;
            Q1=sQuery(id+"F15.wireOp",EDGE,"E36");
            revolve(context, id + "F16", {"operationType" : NewBodyOperationType.REMOVE, "entities" : qUnion([Q0]), "axis" : qUnion([Q1]), "revolveType" : RevolveType.FULL});
        }
        {
            var Q0;
            {var subQ0=sQuery(id+"F0.wireOp",EDGE,"E0.right");var subQ1=sQuery(id+"F0.wireOp",EDGE,"E0.left");var subQ2=sQuery(id+"F0.wireOp",EDGE,"E0.bottom");var subQ3=sQuery(id+"F0.wireOp",EDGE,"E0.top");Q0=makeQuery(id+"F12.boolean.opBoolean","SPLIT",FACE,{"disambiguationData":[TD([makeQuery(id+"F1.opExtrude","SWEPT_FACE",FACE,{"disambiguationData":[OSD([subQ2])]})])],"derivedFrom":makeQuery(id+"F1.opExtrude","CAP_FACE",FACE,{"disambiguationData":[OSD([subQ2,subQ3,subQ1,subQ0])],"isStart":false})});}
            var sketch = newSketch(context, id + "F17", { "sketchPlane" : qUnion([Q0])});
            skLineSegment(sketch, "E37.bottom", {"start": v(36, -28.77) * mm, "end": v(40, -28.77) * mm});
            skLineSegment(sketch, "E37.top", {"start": v(36, -45.77) * mm, "end": v(40, -45.77) * mm});
            skLineSegment(sketch, "E37.left", {"start": v(36, -28.77) * mm, "end": v(36, -45.77) * mm});
            skLineSegment(sketch, "E37.right", {"start": v(40, -28.77) * mm, "end": v(40, -45.77) * mm});
            skSolve(sketch);
        }
        {
            var Q0;
            Q0 = qSketchRegion(id + "F17", true);
            extrude(context, id + "F18", {"entities" : qUnion([Q0]), "operationType" : NewBodyOperationType.REMOVE, "oppositeDirection" : true, "depth" : 1 * mm});
        }
        {
            var Q0;
            Q0=makeQuery(id+"F1.opExtrude","SWEPT_FACE",FACE,{"disambiguationData":[OSD([sQuery(id+"F0.wireOp",EDGE,"E0.left")])]});
            var sketch = newSketch(context, id + "F19", { "sketchPlane" : qUnion([Q0])});
            skLineSegment(sketch, "E38", {"start": v(49.25, 0) * mm, "end": v(44.25, 0) * mm});
            skLineSegment(sketch, "E39", {"start": v(44.25, 0) * mm, "end": v(44.25, 4) * mm});
            skLineSegment(sketch, "E40", {"start": v(44.25, 4) * mm, "end": v(44.25, 5) * mm});
            skLineSegment(sketch, "E41", {"start": v(44.25, 4) * mm, "end": v(49.25, 0) * mm});
            skSolve(sketch);
        }
        {
            var Q0;
            {var subQ0=sQuery(id+"F19.wireOp",EDGE,"E40");Q0=makeQuery(id+"F19.imprint","IMPRINT",FACE,{"disambiguationData":[TD([[makeQuery(id+"F19.imprint","IMPRINT",EDGE,{"derivedFrom":subQ0}),-1.0]])]});}
            extrude(context, id + "F20", {"entities" : qUnion([Q0]), "operationType" : NewBodyOperationType.REMOVE, "oppositeDirection" : true, "depth" : 100 * mm});
        }
    });
